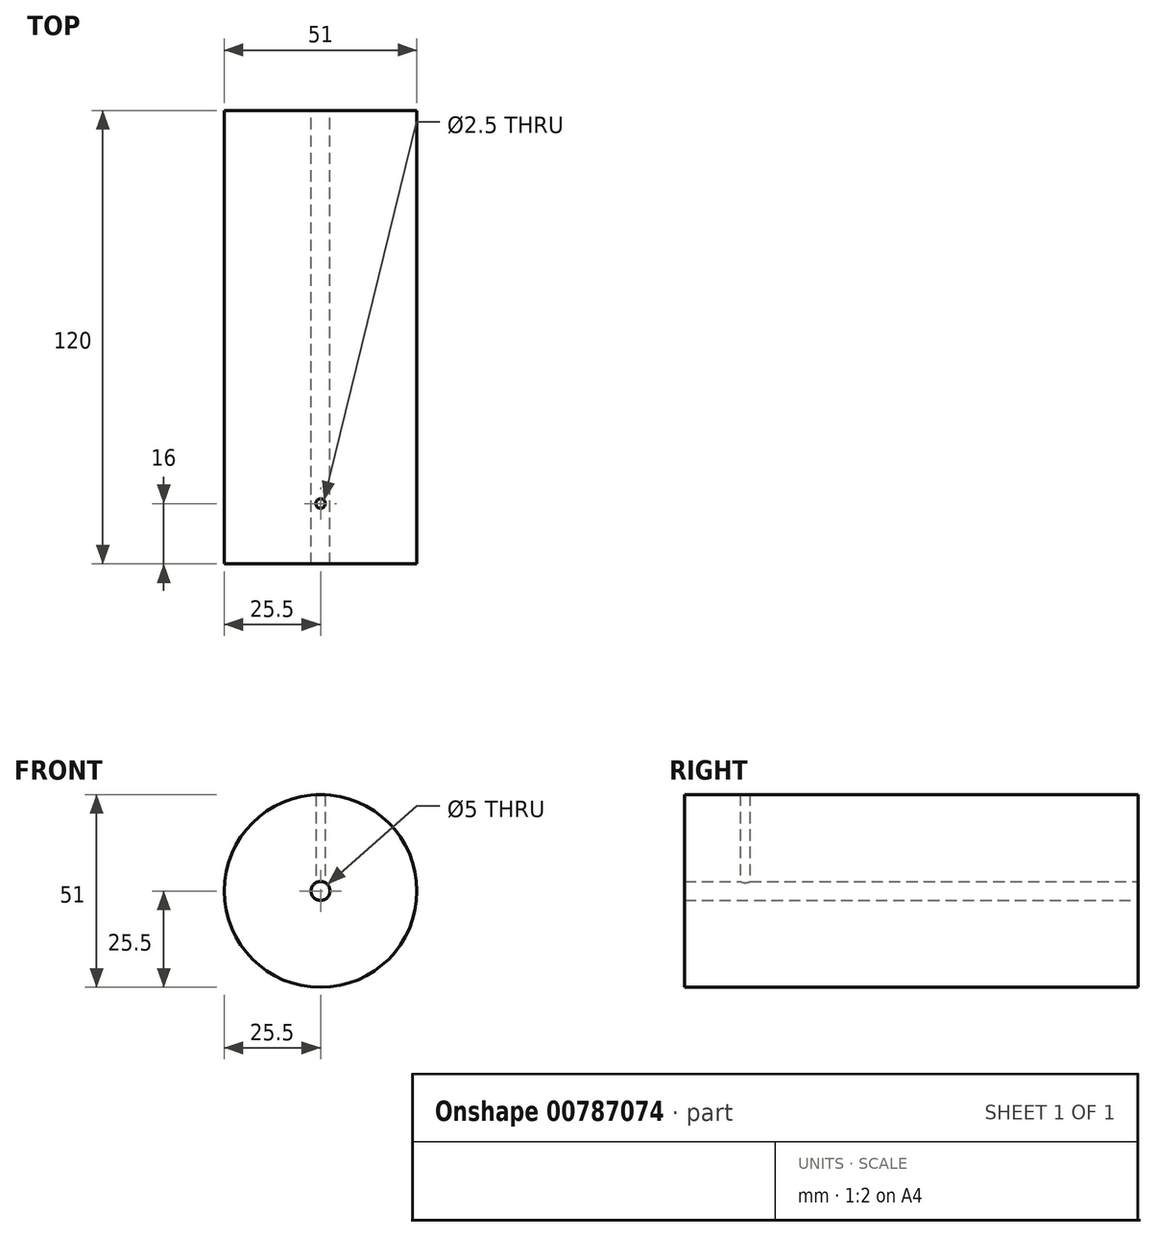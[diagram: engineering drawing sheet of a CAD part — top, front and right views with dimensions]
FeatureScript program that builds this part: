
annotation { "Feature Type Name" : "Feature", "Feature Type Description" : "" }
export const myFeature = defineFeature(function(context is Context, id is Id, definition is map)
    precondition{}
    {
        {
            var Q0;
            Q0=qCreatedBy(makeId("Front.planeOp"),FACE);
            var sketch = newSketch(context, id + "F0", { "sketchPlane" : qUnion([Q0])});
            skCircle(sketch, "E0", {"center": v(0, 0) * mm, "radius": 2.5 * mm});
            skCircle(sketch, "E1", {"center": v(0, 0) * mm, "radius": 25.5 * mm});
            skSolve(sketch);
        }
        {
            var Q0;
            Q0=makeQuery(id+"F0.imprint","IMPRINT",FACE,{"disambiguationData":[TD([[makeQuery(id+"F0.imprint","IMPRINT",EDGE,{"derivedFrom":sQuery(id+"F0.wireOp",EDGE,"E0")}),-1.0]])]});
            var Q1;
            Q1=makeQuery(id+"F0.imprint","IMPRINT",FACE,{"disambiguationData":[TD([[makeQuery(id+"F0.imprint","IMPRINT",EDGE,{"derivedFrom":sQuery(id+"F0.wireOp",EDGE,"E1")}),1.0]])]});
            var Q2;
            {var subQ1=sQuery(id+"F0.wireOp",EDGE,"MV3uiX5v-kzLz-Vt9V-jJa4-cSV4g3sYkiwq.top");Q2=makeQuery(id+"F0.imprint","IMPRINT",FACE,{"disambiguationData":[TD([[makeQuery(id+"F0.imprint","IMPRINT",EDGE,{"derivedFrom":subQ1}),1.0]])]});}
            extrude(context, id + "F1", {"entities" : qUnion([Q0, Q1, Q2]), "depth" : 120 * mm, "offsetDistance" : 25 * mm});
        }
        {
            var Q0;
            Q0=qCreatedBy(makeId("Top.planeOp"),FACE);
            var sketch = newSketch(context, id + "F2", { "sketchPlane" : qUnion([Q0])});
            skPoint(sketch, "E2", {"position": v(0, -104) * mm});
            skSolve(sketch);
        }
        {
            var Q0;
            Q0=sQuery(id+"F2.wireOp",VERTEX,"E2");
            var Q1;
            Q1=makeQuery(id+"F1.opExtrude","SWEPT_BODY",BODY,{"disambiguationData":[OSD([sQuery(id+"F0.wireOp",EDGE,"E0"),sQuery(id+"F0.wireOp",EDGE,"E1")])]});
            hole(context, id + "F3", {"style" : HoleStyle.SIMPLE, "endStyle" : HoleEndStyle.THROUGH, "oppositeDirection" : true, "holeDiameter" : 2.5 * mm, "majorDiameter" : 5 * mm, "isTappedThrough" : true, "tappedDepth" : 12 * mm, "tapClearance" : 3, "startFromSketch" : true, "locations" : qUnion([Q0]), "scope" : qUnion([Q1])});
        }
    });
